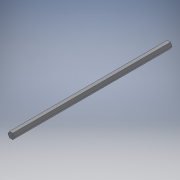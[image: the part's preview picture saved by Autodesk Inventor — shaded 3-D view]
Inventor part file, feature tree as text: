
AUTODESK INVENTOR PART (.ipt)
format: ipt  version: 2018 (Build 220112000, 112)  size: 96,256 bytes
history: native  units: in
note: dims shown in document units (in); Inventor stores cm internally (conversion verified against a paired STEP export)
features: extrude x1, sketch x1
ambient origin geometry x8: Origin, YZ Plane, XZ Plane, XY Plane, X Axis, Y Axis, Z Axis, Center Point
bodies: Solid1 (feature_tree)
feature tree (2):
  extrude  "Extrusion1"  Depth=13.5in TaperAngle=0.0deg
  sketch  "Sketch1"  dims[d0=0.25in d1=13.5in d2=0.0in]
